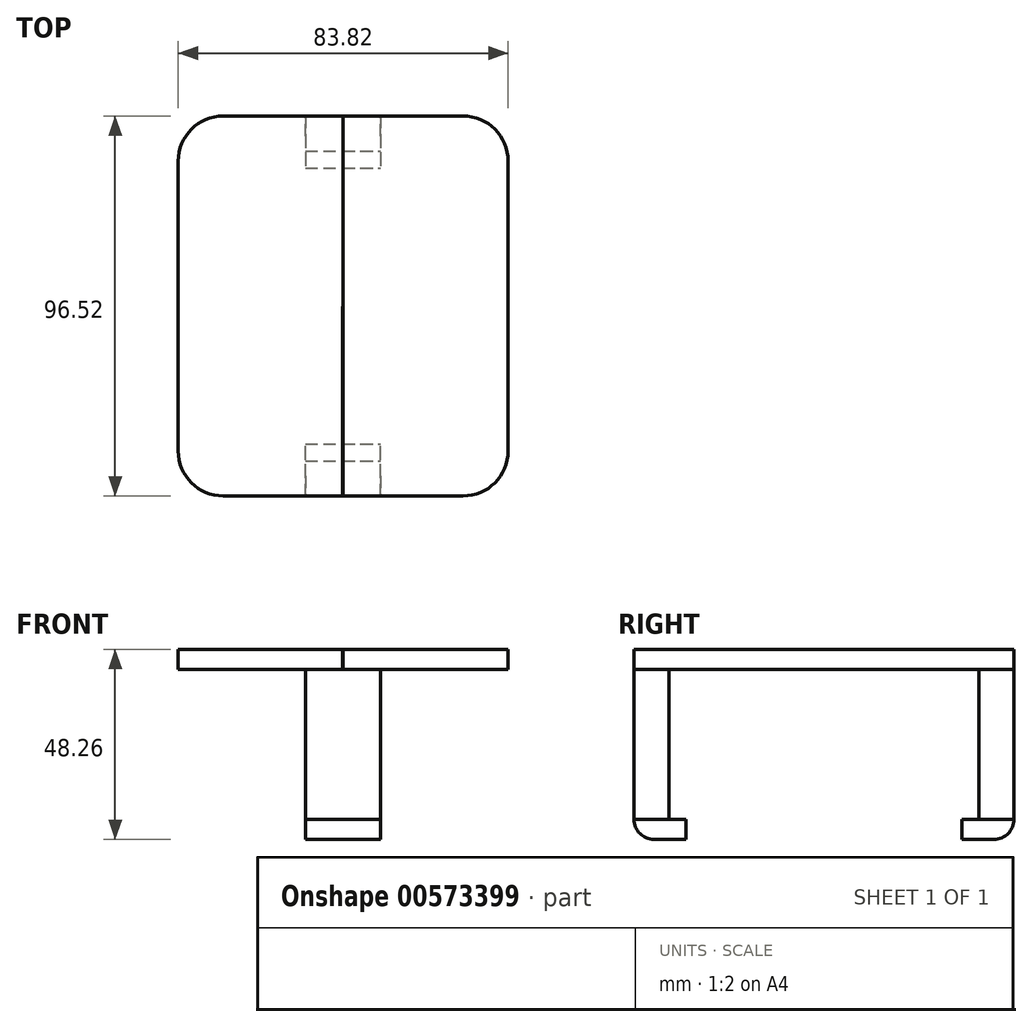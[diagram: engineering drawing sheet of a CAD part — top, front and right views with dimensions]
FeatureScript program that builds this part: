
annotation { "Feature Type Name" : "Feature", "Feature Type Description" : "" }
export const myFeature = defineFeature(function(context is Context, id is Id, definition is map)
    precondition{}
    {
        {
            var Q0;
            Q0=qCreatedBy(makeId("Top.planeOp"),FACE);
            var sketch = newSketch(context, id + "F0", { "sketchPlane" : qUnion([Q0])});
            skLineSegment(sketch, "E0.bottom", {"start": v(-9.35, -17.09) * mm, "end": v(9.7, -17.09) * mm});
            skLineSegment(sketch, "E0.top", {"start": v(-9.35, -3.88) * mm, "end": v(9.7, -3.88) * mm});
            skLineSegment(sketch, "E0.left", {"start": v(-9.35, -17.09) * mm, "end": v(-9.35, -3.88) * mm});
            skLineSegment(sketch, "E0.right", {"start": v(9.7, -17.09) * mm, "end": v(9.7, -3.88) * mm});
            skLineSegment(sketch, "E1", {"start": v(-33.9, 31.17) * mm, "end": v(43.44, 31.17) * mm});
            skLineSegment(sketch, "E2.MirrorCS", {"start": v(9.7, 79.43) * mm, "end": v(9.7, 66.23) * mm});
            skLineSegment(sketch, "E3.MirrorCS", {"start": v(-9.35, 79.43) * mm, "end": v(-9.35, 66.23) * mm});
            skLineSegment(sketch, "E4.MirrorCS", {"start": v(-9.35, 66.23) * mm, "end": v(9.7, 66.23) * mm});
            skLineSegment(sketch, "E5.MirrorCS", {"start": v(-9.35, 79.43) * mm, "end": v(9.7, 79.43) * mm});
            skSolve(sketch);
        }
        {
            var Q0;
            Q0 = qSketchRegion(id + "F0", true);
            extrude(context, id + "F1", {"entities" : qUnion([Q0]), "depth" : 5.08 * mm, "offsetDistance" : 25.4 * mm});
        }
        {
            var Q0;
            Q0=makeQuery(id+"F1.opExtrude","CAP_FACE",FACE,{"disambiguationData":[OSD([sQuery(id+"F0.wireOp",EDGE,"E0.bottom"),sQuery(id+"F0.wireOp",EDGE,"E0.top"),sQuery(id+"F0.wireOp",EDGE,"E0.left"),sQuery(id+"F0.wireOp",EDGE,"E0.right")])],"isStart":false});
            var sketch = newSketch(context, id + "F2", { "sketchPlane" : qUnion([Q0])});
            skLineSegment(sketch, "E6.bottom", {"start": v(-9.35, -17.09) * mm, "end": v(9.7, -17.09) * mm});
            skLineSegment(sketch, "E6.top", {"start": v(-9.35, -8.2) * mm, "end": v(9.7, -8.2) * mm});
            skLineSegment(sketch, "E6.left", {"start": v(-9.35, -17.09) * mm, "end": v(-9.35, -8.2) * mm});
            skLineSegment(sketch, "E6.right", {"start": v(9.7, -17.09) * mm, "end": v(9.7, -8.2) * mm});
            skLineSegment(sketch, "E7", {"start": v(-31.1, 31.17) * mm, "end": v(42.28, 31.17) * mm});
            skLineSegment(sketch, "E8.MirrorCS", {"start": v(9.7, 79.43) * mm, "end": v(9.7, 70.54) * mm});
            skLineSegment(sketch, "E9.MirrorCS", {"start": v(-9.35, 79.43) * mm, "end": v(9.7, 79.43) * mm});
            skLineSegment(sketch, "E10.MirrorCS", {"start": v(-9.35, 79.43) * mm, "end": v(-9.35, 70.54) * mm});
            skLineSegment(sketch, "E11.MirrorCS", {"start": v(-9.35, 70.54) * mm, "end": v(9.7, 70.54) * mm});
            skSolve(sketch);
        }
        {
            var Q0;
            Q0 = qSketchRegion(id + "F2", true);
            extrude(context, id + "F3", {"entities" : qUnion([Q0]), "depth" : 38.1 * mm, "offsetDistance" : 25.4 * mm});
        }
        {
            var Q0;
            Q0=makeQuery(id+"F3.opExtrude","CAP_FACE",FACE,{"disambiguationData":[OSD([sQuery(id+"F2.wireOp",EDGE,"E8.MirrorCS"),sQuery(id+"F2.wireOp",EDGE,"E9.MirrorCS"),sQuery(id+"F2.wireOp",EDGE,"E10.MirrorCS"),sQuery(id+"F2.wireOp",EDGE,"E11.MirrorCS")])],"isStart":false});
            var sketch = newSketch(context, id + "F4", { "sketchPlane" : qUnion([Q0])});
            skLineSegment(sketch, "E12", {"start": v(0.17, 79.43) * mm, "end": v(0, -17.1) * mm});
            skLineSegment(sketch, "E13.bottom", {"start": v(0.17, 79.43) * mm, "end": v(-41.74, 79.43) * mm});
            skLineSegment(sketch, "E13.top", {"start": v(0.17, -17.09) * mm, "end": v(-41.74, -17.09) * mm});
            skLineSegment(sketch, "E13.left", {"start": v(0.17, 79.43) * mm, "end": v(0.17, -17.09) * mm});
            skLineSegment(sketch, "E13.right", {"start": v(-41.74, 79.43) * mm, "end": v(-41.74, -17.09) * mm});
            skLineSegment(sketch, "E14.MirrorCS", {"start": v(42.08, 79.43) * mm, "end": v(42.08, -17.09) * mm});
            skLineSegment(sketch, "E15.MirrorCS", {"start": v(0.17, -17.09) * mm, "end": v(42.08, -17.09) * mm});
            skLineSegment(sketch, "E16.MirrorCS", {"start": v(0.17, 79.43) * mm, "end": v(42.08, 79.43) * mm});
            skSolve(sketch);
        }
        {
            var Q0;
            {var subQ2=sQuery(id+"F4.wireOp",EDGE,"E14.MirrorCS");Q0=makeQuery(id+"F4.imprint","IMPRINT",FACE,{"disambiguationData":[TD([[makeQuery(id+"F4.imprint","IMPRINT",EDGE,{"derivedFrom":subQ2}),-1.0]])]});}
            var Q1;
            {var subQ0=sQuery(id+"F4.wireOp",EDGE,"E13.right");Q1=makeQuery(id+"F4.imprint","IMPRINT",FACE,{"disambiguationData":[TD([[makeQuery(id+"F4.imprint","IMPRINT",EDGE,{"derivedFrom":subQ0}),1.0]])]});}
            var Q2;
            {var subQ5=makeQuery(id+"F3.opExtrude","CAP_EDGE",EDGE,{"disambiguationData":[OSD([sQuery(id+"F2.wireOp",EDGE,"E10.MirrorCS")])],"isStart":false});Q2=makeQuery(id+"F4.imprint","IMPRINT",FACE,{"disambiguationData":[TD([[makeQuery(id+"F4.imprint","IMPRINT",EDGE,{"derivedFrom":subQ5}),1.0]])]});}
            var Q3;
            {var subQ5=makeQuery(id+"F3.opExtrude","CAP_EDGE",EDGE,{"disambiguationData":[OSD([sQuery(id+"F2.wireOp",EDGE,"E8.MirrorCS")])],"isStart":false});Q3=makeQuery(id+"F4.imprint","IMPRINT",FACE,{"disambiguationData":[TD([[makeQuery(id+"F4.imprint","IMPRINT",EDGE,{"derivedFrom":subQ5}),-1.0]])]});}
            extrude(context, id + "F5", {"entities" : qUnion([Q0, Q1, Q2, Q3]), "depth" : 5.08 * mm, "offsetDistance" : 25.4 * mm});
        }
        {
            var Q0;
            Q0=makeQuery(id+"F1.opExtrude","CAP_EDGE",EDGE,{"disambiguationData":[OSD([sQuery(id+"F0.wireOp",EDGE,"E5.MirrorCS")])],"isStart":true});
            var Q1;
            Q1=makeQuery(id+"F1.opExtrude","CAP_EDGE",EDGE,{"disambiguationData":[OSD([sQuery(id+"F0.wireOp",EDGE,"E0.bottom")])],"isStart":true});
            fillet(context, id + "F6", {"entities" : qUnion([Q0, Q1]), "radius" : 5.08 * mm, "tangentPropagation" : true, "allowEdgeOverflow" : false});
        }
        {
            var Q0;
            Q0=makeQuery(id+"F5.opExtrude","SWEPT_EDGE",EDGE,{"disambiguationData":[OSD([sQuery(id+"F4.wireOp",EDGE,"E14.MirrorCS"),sQuery(id+"F4.wireOp",EDGE,"E16.MirrorCS")])]});
            var Q1;
            Q1=makeQuery(id+"F5.opExtrude","SWEPT_EDGE",EDGE,{"disambiguationData":[OSD([sQuery(id+"F4.wireOp",EDGE,"E13.bottom"),sQuery(id+"F4.wireOp",EDGE,"E13.right")])]});
            var Q2;
            Q2=makeQuery(id+"F5.opExtrude","SWEPT_EDGE",EDGE,{"disambiguationData":[OSD([sQuery(id+"F4.wireOp",EDGE,"E13.top"),sQuery(id+"F4.wireOp",EDGE,"E13.right")])]});
            var Q3;
            Q3=makeQuery(id+"F5.opExtrude","SWEPT_EDGE",EDGE,{"disambiguationData":[OSD([sQuery(id+"F4.wireOp",EDGE,"E14.MirrorCS"),sQuery(id+"F4.wireOp",EDGE,"E15.MirrorCS")])]});
            fillet(context, id + "F7", {"entities" : qUnion([Q0, Q1, Q2, Q3]), "radius" : 11.43 * mm, "tangentPropagation" : true, "allowEdgeOverflow" : false});
        }
    });
